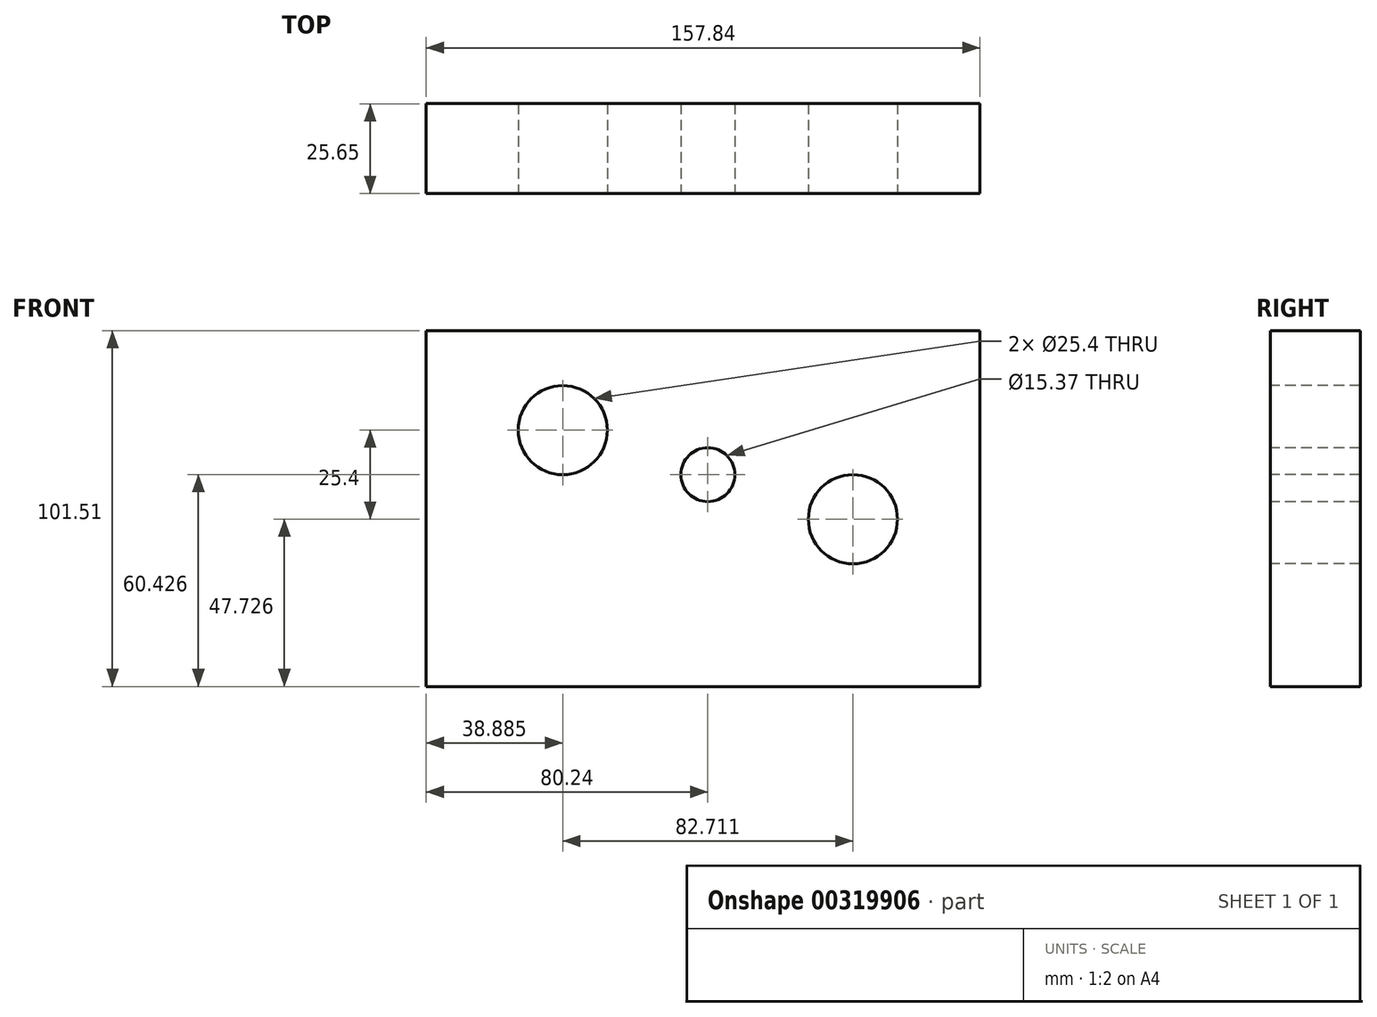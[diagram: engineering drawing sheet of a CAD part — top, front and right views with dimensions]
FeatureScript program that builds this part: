
annotation { "Feature Type Name" : "Feature", "Feature Type Description" : "" }
export const myFeature = defineFeature(function(context is Context, id is Id, definition is map)
    precondition{}
    {
        {
            var Q0;
            Q0=qCreatedBy(makeId("Front.planeOp"),FACE);
            var sketch = newSketch(context, id + "F0", { "sketchPlane" : qUnion([Q0])});
            skLineSegment(sketch, "E0.bottom", {"start": v(0, 0) * mm, "end": v(157.84, 0) * mm});
            skLineSegment(sketch, "E0.top", {"start": v(0, 101.51) * mm, "end": v(157.84, 101.51) * mm});
            skLineSegment(sketch, "E0.left", {"start": v(0, 0) * mm, "end": v(0, 101.51) * mm});
            skLineSegment(sketch, "E0.right", {"start": v(157.84, 0) * mm, "end": v(157.84, 101.51) * mm});
            skSolve(sketch);
        }
        {
            var Q0;
            Q0 = qSketchRegion(id + "F0", true);
            extrude(context, id + "F1", {"entities" : qUnion([Q0]), "oppositeDirection" : true, "depth" : 25.65 * mm});
        }
        {
            var Q0;
            Q0=makeQuery(id+"F1.opExtrude","CAP_FACE",FACE,{"disambiguationData":[OSD([sQuery(id+"F0.wireOp",EDGE,"E0.bottom"),sQuery(id+"F0.wireOp",EDGE,"E0.top"),sQuery(id+"F0.wireOp",EDGE,"E0.left"),sQuery(id+"F0.wireOp",EDGE,"E0.right")])],"isStart":true});
            var sketch = newSketch(context, id + "F2", { "sketchPlane" : qUnion([Q0])});
            skCircle(sketch, "E1", {"center": v(38.88, 73.13) * mm, "radius": 12.7 * mm});
            skCircle(sketch, "E2", {"center": v(121.6, 47.73) * mm, "radius": 12.7 * mm});
            skLineSegment(sketch, "E3", {"start": v(38.88, 60.43) * mm, "end": v(121.6, 60.43) * mm, "construction": true});
            skCircle(sketch, "E4", {"center": v(80.24, 60.43) * mm, "radius": 7.68 * mm});
            skSolve(sketch);
        }
        {
            var Q0;
            Q0 = qSketchRegion(id + "F2", true);
            extrude(context, id + "F3", {"entities" : qUnion([Q0]), "operationType" : NewBodyOperationType.REMOVE, "endBound" : BoundingType.THROUGH_ALL, "oppositeDirection" : true, "depth" : 25.4 * mm});
        }
    });
